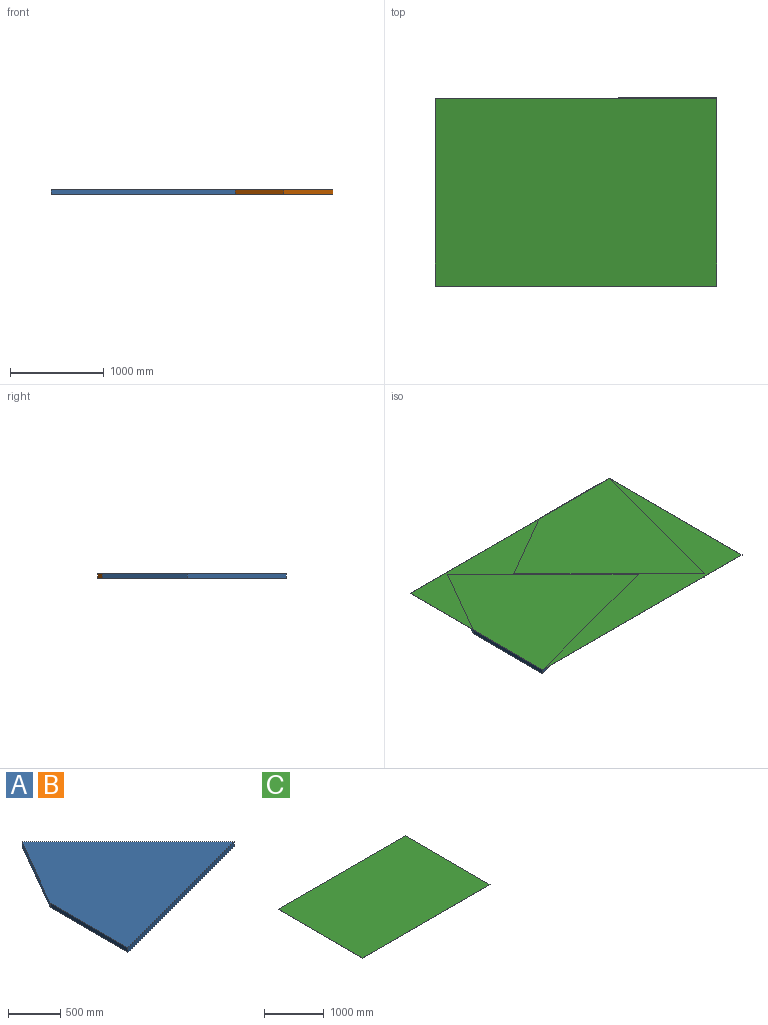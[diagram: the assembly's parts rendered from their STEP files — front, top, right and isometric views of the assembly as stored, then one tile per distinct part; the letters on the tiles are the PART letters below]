
ASSEMBLY  parts=3 mates=1
PART A: 6 faces, bbox 1960x1960x50 mm
  f0: plane 1434.82x1434.82mm, normal (0.71,0.71,0), area 101457.1mm2, adj f1,f3,f4,f5
  f1: plane 909.64x525.18mm, normal (-0.87,0.5,0), area 52518mm2, adj f0,f2,f4,f5
  f2: plane 1050.36x50mm, normal (-1,0,0), area 52518mm2, adj f1,f3,f4,f5
  f3: plane 1960x525.18mm, normal (0.26,-0.97,0), area 101457.1mm2, adj f0,f2,f4,f5
  f4: plane 1960x1960mm, normal (0,0,1), area 2058707.2mm2, adj f0,f1,f2,f3
  f5: plane 1960x1960mm, normal (0,0,-1), area 2058707.2mm2, adj f0,f1,f2,f3
PART B: same geometry as A
PART C: 6 faces, bbox 3000x2000x2 mm
  f0: plane 3000x2mm, normal (0,1,0), area 6000mm2, adj f1,f3,f4,f5
  f1: plane 2000x2mm, normal (-1,0,0), area 4000mm2, adj f0,f2,f4,f5
  f2: plane 3000x2mm, normal (0,-1,0), area 6000mm2, adj f1,f3,f4,f5
  f3: plane 2000x2mm, normal (1,0,0), area 4000mm2, adj f0,f2,f4,f5
  f4: plane 3000x2000mm, normal (0,0,1), area 6000000mm2, adj f0,f1,f2,f3
  f5: plane 3000x2000mm, normal (0,0,-1), area 6000000mm2, adj f0,f1,f2,f3
PLACE A t=(2314.69,-834.81,-1981.87)mm
PLACE B rot(axis=(0,0,-1),60deg) t=(2832.39,-1315.75,-1981.87)mm
PLACE C t=(1854.69,-359.99,-1931.87)mm
MATE fastened A.f4 <-> C.f5  axis (0,0,1) through (354.69,-1359.99,-1931.87)mm
